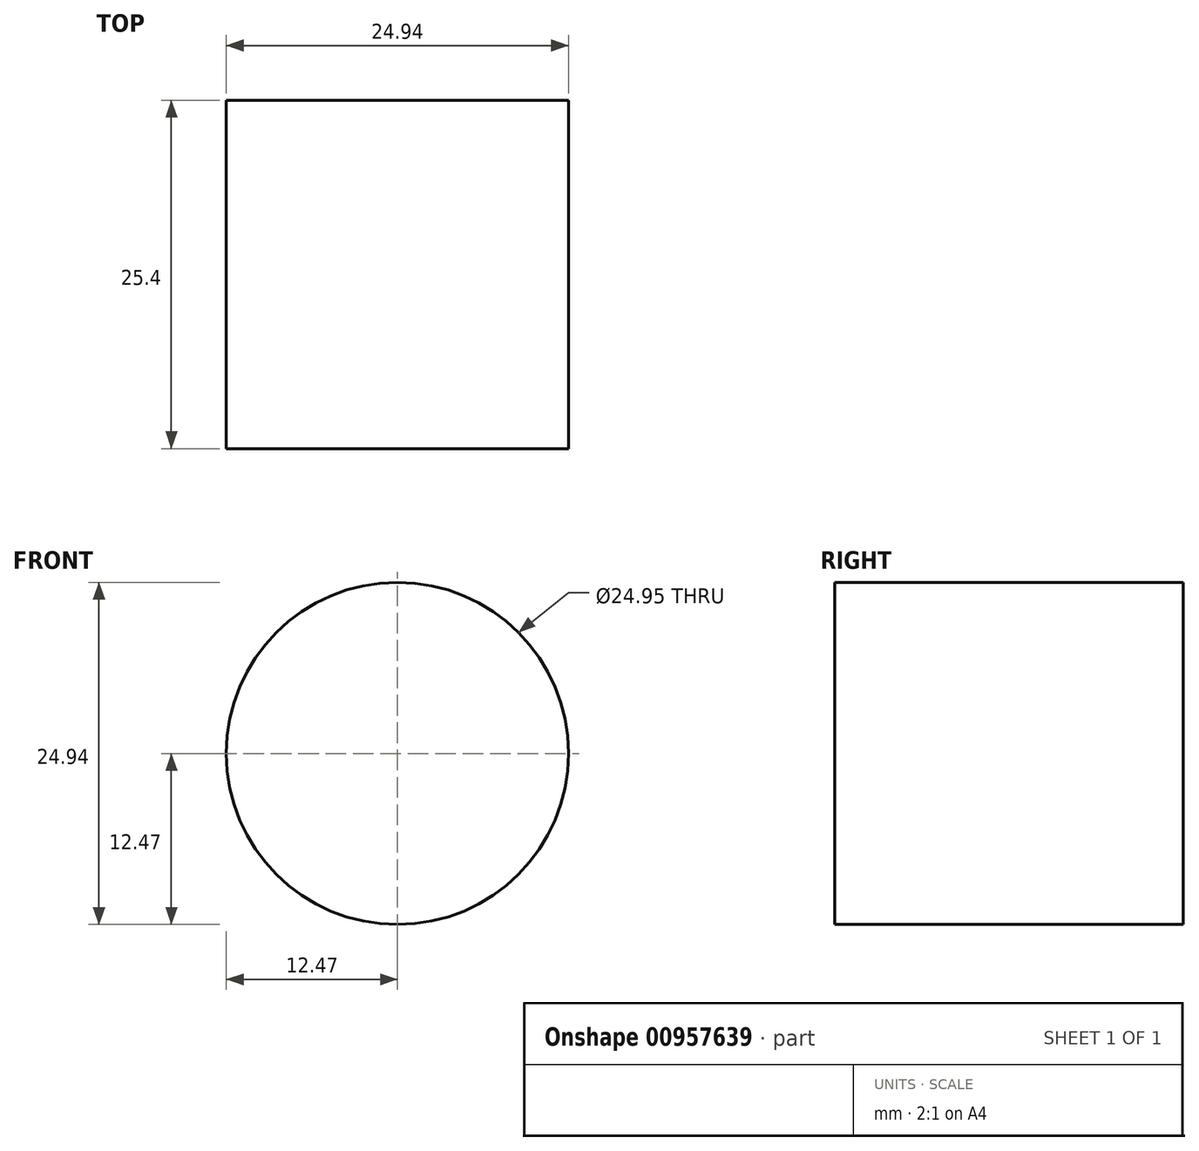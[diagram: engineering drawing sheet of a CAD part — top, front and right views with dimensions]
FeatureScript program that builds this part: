
annotation { "Feature Type Name" : "Feature", "Feature Type Description" : "" }
export const myFeature = defineFeature(function(context is Context, id is Id, definition is map)
    precondition{}
    {
        {
            var Q0;
            Q0=qCreatedBy(makeId("Front.planeOp"),FACE);
            var sketch = newSketch(context, id + "F0", { "sketchPlane" : qUnion([Q0])});
            skLineSegment(sketch, "E0", {"start": v(0, 56.46) * mm, "end": v(0, -42.07) * mm});
            skLineSegment(sketch, "E1", {"start": v(0, -42.07) * mm, "end": v(62.37, -42.07) * mm});
            skCircle(sketch, "E2", {"center": v(0, 0) * mm, "radius": 13.31 * mm});
            skCircle(sketch, "E3", {"center": v(0, 56.46) * mm, "radius": 12.47 * mm});
            skCircle(sketch, "E4", {"center": v(0, -42.07) * mm, "radius": 14.57 * mm});
            skCircle(sketch, "E5", {"center": v(62.37, -42.07) * mm, "radius": 10.95 * mm});
            skSolve(sketch);
        }
        {
            var Q0;
            Q0=sQuery(id+"F0.wireOp",EDGE,"E3");
            extrude(context, id + "F1", {"bodyType" : ToolBodyType.SURFACE, "surfaceEntities" : qUnion([Q0]), "oppositeDirection" : true, "depth" : 25.4 * mm, "offsetDistance" : 25.4 * mm});
        }
    });
